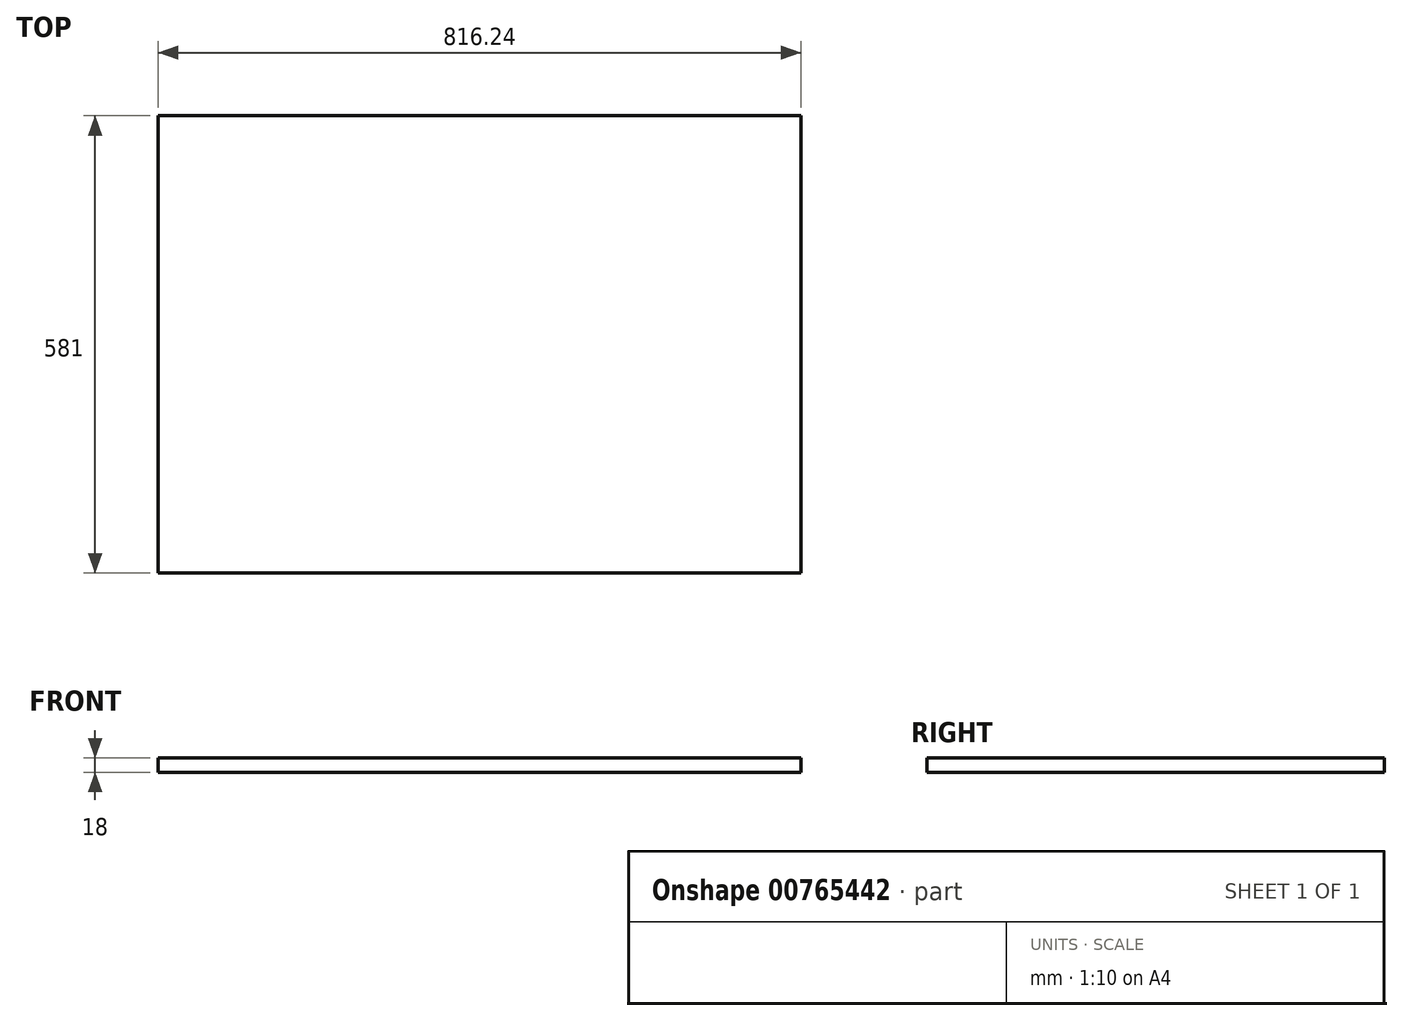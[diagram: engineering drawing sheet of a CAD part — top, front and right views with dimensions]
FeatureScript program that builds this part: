
annotation { "Feature Type Name" : "Feature", "Feature Type Description" : "" }
export const myFeature = defineFeature(function(context is Context, id is Id, definition is map)
    precondition{}
    {
        {
            var Q0;
            Q0=qCreatedBy(makeId("Top.planeOp"),FACE);
            var sketch = newSketch(context, id + "F0", { "sketchPlane" : qUnion([Q0])});
            skLineSegment(sketch, "E0.bottom", {"start": v(-408.12, -290.5) * mm, "end": v(408.13, -290.5) * mm});
            skLineSegment(sketch, "E0.top", {"start": v(-408.12, 290.5) * mm, "end": v(408.12, 290.5) * mm});
            skLineSegment(sketch, "E0.left", {"start": v(-408.12, -290.5) * mm, "end": v(-408.12, 290.5) * mm});
            skLineSegment(sketch, "E0.right", {"start": v(408.12, -290.5) * mm, "end": v(408.12, 290.5) * mm});
            skPoint(sketch, "E0.middle", {"position": v(0, 0) * mm});
            skSolve(sketch);
        }
        {
            var Q0;
            Q0 = qSketchRegion(id + "F0", true);
            extrude(context, id + "F1", {"entities" : qUnion([Q0]), "depth" : 18 * mm, "offsetDistance" : 25 * mm});
        }
    });
